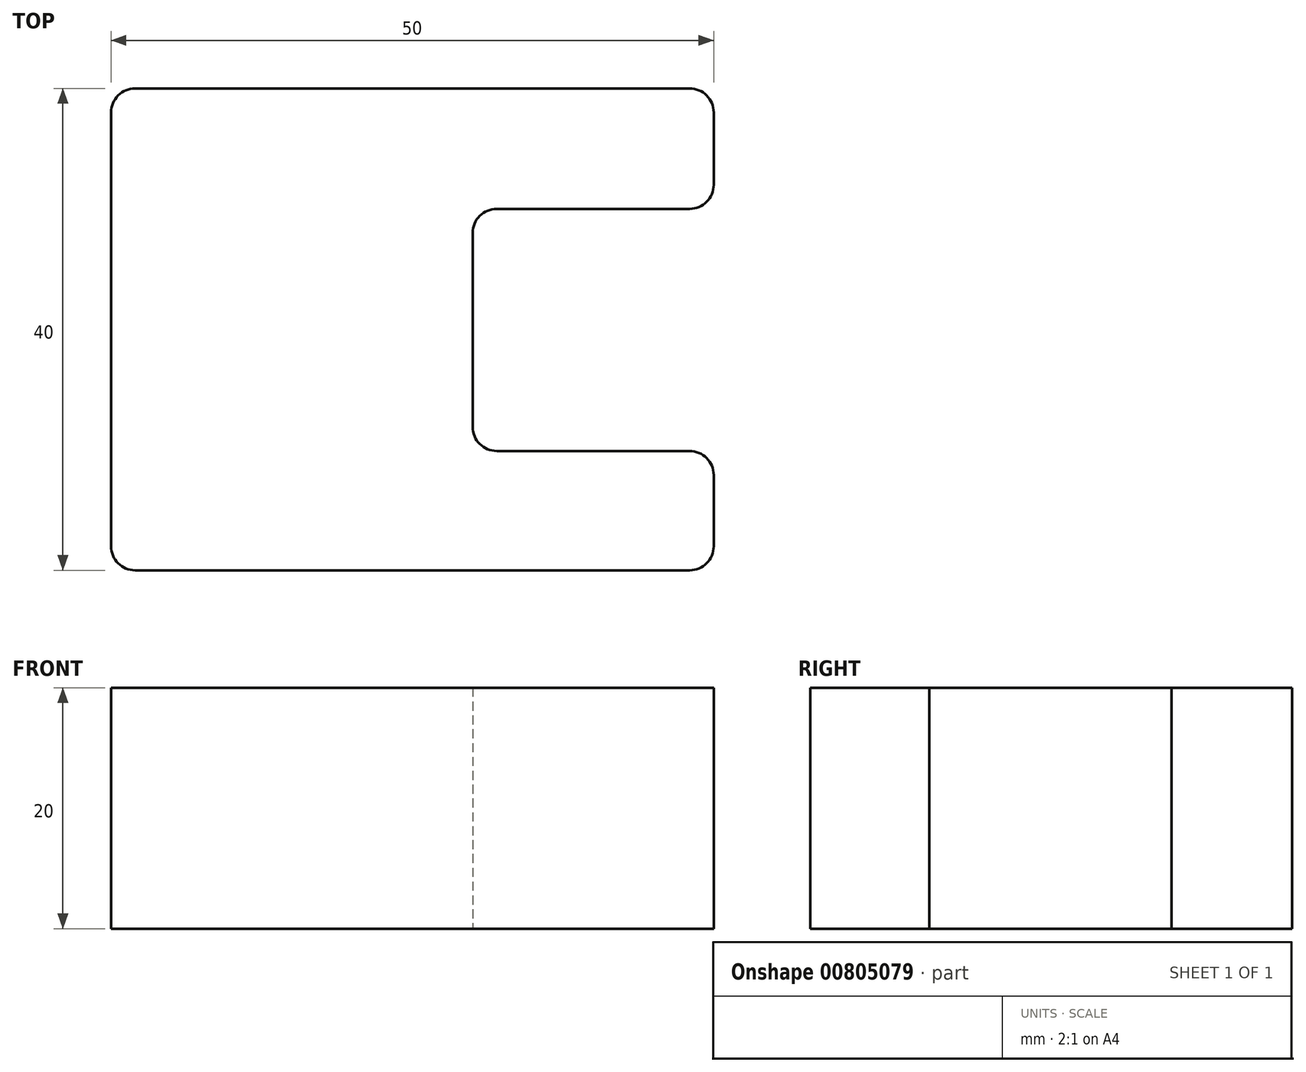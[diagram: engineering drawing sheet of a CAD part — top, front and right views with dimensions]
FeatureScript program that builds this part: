
annotation { "Feature Type Name" : "Feature", "Feature Type Description" : "" }
export const myFeature = defineFeature(function(context is Context, id is Id, definition is map)
    precondition{}
    {
        {
            var Q0;
            Q0=qCreatedBy(makeId("Top.planeOp"),FACE);
            var sketch = newSketch(context, id + "F0", { "sketchPlane" : qUnion([Q0])});
            skLineSegment(sketch, "E0", {"start": v(0, 0) * mm, "end": v(0, 40) * mm});
            skLineSegment(sketch, "E1", {"start": v(0, 40) * mm, "end": v(50, 40) * mm});
            skLineSegment(sketch, "E2", {"start": v(50, 40) * mm, "end": v(50, 30) * mm});
            skLineSegment(sketch, "E3", {"start": v(50, 30) * mm, "end": v(30, 30) * mm});
            skLineSegment(sketch, "E4", {"start": v(30, 30) * mm, "end": v(30, 9.9) * mm});
            skLineSegment(sketch, "E5", {"start": v(30, 9.9) * mm, "end": v(50, 9.9) * mm});
            skLineSegment(sketch, "E6", {"start": v(50, 9.9) * mm, "end": v(50, 0) * mm});
            skLineSegment(sketch, "E7", {"start": v(50, 0) * mm, "end": v(0, 0) * mm});
            skSolve(sketch);
        }
        {
            var Q0;
            Q0=makeQuery(id+"F0.imprint","IMPRINT",FACE,{"disambiguationData":[TD([[makeQuery(id+"F0.imprint","IMPRINT",EDGE,{"derivedFrom":sQuery(id+"F0.wireOp",EDGE,"E0")}),-1.0]])]});
            extrude(context, id + "F1", {"entities" : qUnion([Q0]), "depth" : 20 * mm, "offsetDistance" : 25 * mm});
        }
        {
            var Q0;
            Q0=makeQuery(id+"F1.opExtrude","SWEPT_EDGE",EDGE,{"disambiguationData":[OSD([sQuery(id+"F0.wireOp",EDGE,"E0"),sQuery(id+"F0.wireOp",EDGE,"E7")])]});
            var Q1;
            Q1=makeQuery(id+"F1.opExtrude","SWEPT_EDGE",EDGE,{"disambiguationData":[OSD([sQuery(id+"F0.wireOp",EDGE,"E6"),sQuery(id+"F0.wireOp",EDGE,"E7")])]});
            var Q2;
            Q2=makeQuery(id+"F1.opExtrude","SWEPT_EDGE",EDGE,{"disambiguationData":[OSD([sQuery(id+"F0.wireOp",EDGE,"E5"),sQuery(id+"F0.wireOp",EDGE,"E6")])]});
            var Q3;
            Q3=makeQuery(id+"F1.opExtrude","SWEPT_EDGE",EDGE,{"disambiguationData":[OSD([sQuery(id+"F0.wireOp",EDGE,"E4"),sQuery(id+"F0.wireOp",EDGE,"E5")])]});
            var Q4;
            Q4=makeQuery(id+"F1.opExtrude","SWEPT_EDGE",EDGE,{"disambiguationData":[OSD([sQuery(id+"F0.wireOp",EDGE,"E3"),sQuery(id+"F0.wireOp",EDGE,"E4")])]});
            var Q5;
            Q5=makeQuery(id+"F1.opExtrude","SWEPT_EDGE",EDGE,{"disambiguationData":[OSD([sQuery(id+"F0.wireOp",EDGE,"E2"),sQuery(id+"F0.wireOp",EDGE,"E3")])]});
            var Q6;
            Q6=makeQuery(id+"F1.opExtrude","SWEPT_EDGE",EDGE,{"disambiguationData":[OSD([sQuery(id+"F0.wireOp",EDGE,"E1"),sQuery(id+"F0.wireOp",EDGE,"E2")])]});
            var Q7;
            Q7=makeQuery(id+"F1.opExtrude","SWEPT_EDGE",EDGE,{"disambiguationData":[OSD([sQuery(id+"F0.wireOp",EDGE,"E0"),sQuery(id+"F0.wireOp",EDGE,"E1")])]});
            fillet(context, id + "F2", {"entities" : qUnion([Q0, Q1, Q2, Q3, Q4, Q5, Q6, Q7]), "radius" : 2 * mm, "tangentPropagation" : true, "allowEdgeOverflow" : false});
        }
    });
